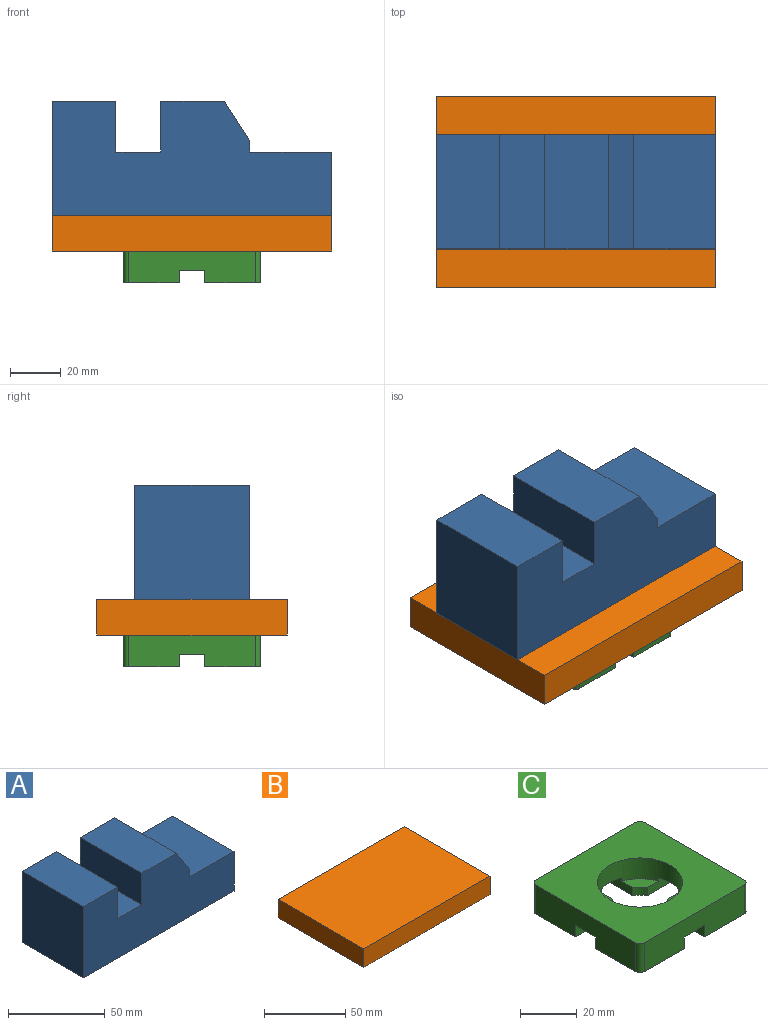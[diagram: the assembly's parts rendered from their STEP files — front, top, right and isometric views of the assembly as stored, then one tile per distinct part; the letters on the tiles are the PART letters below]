
ASSEMBLY  parts=3 mates=2
PART A: 13 faces, bbox 110x45x45 mm
  f0: plane 110x45mm, normal (0,0,-1), area 4950mm2, adj f1,f10,f11,f12
  f1: plane 45x25mm, normal (1,0,0), area 1125mm2, adj f0,f2,f11,f12
  f2: plane 45x32.3mm, normal (0,0,1), area 1453.6mm2, adj f1,f3,f11,f12
  f3: plane 45x4.59mm, normal (1,0,0), area 206.5mm2, adj f2,f4,f11,f12
  f4: plane 45x15.41mm, normal (0.84,0,0.54), area 824.9mm2, adj f3,f5,f11,f12
  f5: plane 45x25.08mm, normal (0,0,1), area 1128.4mm2, adj f4,f6,f11,f12
  f6: plane 45x20mm, normal (-1,0,0), area 900mm2, adj f5,f7,f11,f12
  f7: plane 45x17.7mm, normal (0,0,1), area 796.4mm2, adj f6,f8,f11,f12
  f8: plane 45x20mm, normal (1,0,0), area 900mm2, adj f7,f9,f11,f12
  f9: plane 45x25mm, normal (0,0,1), area 1125mm2, adj f8,f10,f11,f12
  f10: plane 45x45mm, normal (-1,0,0), area 2025mm2, adj f0,f9,f11,f12
  f11: plane 110x45mm, normal (0,-1,0), area 3873.5mm2, adj f0,f1,f2,f3,f4,f5,f6,f7
  f12: plane 110x45mm, normal (0,1,0), area 3873.5mm2, adj f0,f1,f2,f3,f4,f5,f6,f7
PART B: 6 faces, bbox 110x75x14 mm
  f0: plane 75x14mm, normal (-1,0,0), area 1050mm2, adj f1,f3,f4,f5
  f1: plane 110x14mm, normal (0,-1,0), area 1540mm2, adj f0,f2,f4,f5
  f2: plane 75x14mm, normal (1,0,0), area 1050mm2, adj f1,f3,f4,f5
  f3: plane 110x14mm, normal (0,1,0), area 1540mm2, adj f0,f2,f4,f5
  f4: plane 110x75mm, normal (0,0,1), area 8250mm2, adj f0,f1,f2,f3
  f5: plane 110x75mm, normal (0,0,-1), area 8250mm2, adj f0,f1,f2,f3
PART C: 34 faces, bbox 54x54x12.5 mm
  f0: cylinder r=10mm len=3.66mm, axis (0,0,-1), area 18.3mm2, adj f5,f10,f17,f26
  f1: cylinder r=10mm len=3.66mm, axis (0,0,-1), area 18.3mm2, adj f4,f15,f16,f27
  f2: cylinder r=10mm len=3.66mm, axis (0,0,-1), area 18.3mm2, adj f6,f9,f18,f28
  f3: cylinder r=10mm len=3.66mm, axis (0,0,-1), area 18.3mm2, adj f7,f8,f11,f29
  f4: plane 22x22mm, normal (0,0,-1), area 475.3mm2, adj f1,f15,f16,f20,f22,f33
  f5: plane 22x22mm, normal (0,0,-1), area 475.3mm2, adj f0,f10,f17,f21,f22,f32
  f6: plane 22x22mm, normal (0,0,-1), area 475.3mm2, adj f2,f9,f18,f19,f20,f30
  f7: plane 22x22mm, normal (0,0,-1), area 475.3mm2, adj f3,f8,f11,f19,f21,f31
  f8: plane 18.34x5mm, normal (-1,0,0), area 83.5mm2, adj f3,f7,f12,f19,f25,f29
  f9: plane 18.34x5mm, normal (1,0,0), area 83.5mm2, adj f2,f6,f12,f19,f25,f28
  f10: plane 18.34x5mm, normal (0,-1,0), area 83.5mm2, adj f0,f5,f13,f21,f25,f26
  f11: plane 18.34x5mm, normal (0,1,0), area 83.5mm2, adj f3,f7,f13,f21,f25,f29
  f12: plane 12.86x10mm, normal (0,0,-1), area 122.8mm2, adj f8,f9,f19,f25
  f13: plane 12.86x10mm, normal (0,0,-1), area 122.8mm2, adj f10,f11,f21,f25
  f14: plane 12.86x10mm, normal (0,0,-1), area 122.8mm2, adj f16,f17,f22,f25
  f15: plane 18.34x5mm, normal (0,-1,0), area 83.5mm2, adj f1,f4,f20,f24,f25,f27
  f16: plane 18.34x5mm, normal (1,0,0), area 83.5mm2, adj f1,f4,f14,f22,f25,f27
  f17: plane 18.34x5mm, normal (-1,0,0), area 83.5mm2, adj f0,f5,f14,f22,f25,f26
  f18: plane 18.34x5mm, normal (0,1,0), area 83.5mm2, adj f2,f6,f20,f24,f25,f28
  f19: plane 50x12.5mm, normal (0,-1,0), area 575mm2, adj f6,f7,f8,f9,f12,f23,f30,f31
  f20: plane 50x12.5mm, normal (-1,0,0), area 575mm2, adj f4,f6,f15,f18,f23,f24,f30,f33
  f21: plane 50x12.5mm, normal (1,0,0), area 575mm2, adj f5,f7,f10,f11,f13,f23,f31,f32
  f22: plane 50x12.5mm, normal (0,1,0), area 575mm2, adj f4,f5,f14,f16,f17,f23,f32,f33
  f23: plane 54x54mm, normal (0,0,1), area 2205.7mm2, adj f19,f20,f21,f22,f25,f30,f31,f32
  f24: plane 12.86x10mm, normal (0,0,-1), area 122.8mm2, adj f15,f18,f20,f25
  f25: cylinder r=15mm len=30mm, axis (0,0,1), area 787.1mm2, adj f8,f9,f10,f11,f12,f13,f14,f15
  f26: plane 9.14x9.14mm, normal (0,0,1), area 46.7mm2, adj f0,f10,f17,f25
  f27: plane 9.14x9.14mm, normal (0,0,1), area 46.7mm2, adj f1,f15,f16,f25
  f28: plane 9.14x9.14mm, normal (0,0,1), area 46.7mm2, adj f2,f9,f18,f25
  f29: plane 9.14x9.14mm, normal (0,0,1), area 46.7mm2, adj f3,f8,f11,f25
  f30: cylinder r=2mm len=12.5mm, axis (0,0,1), area 39.3mm2, adj f6,f19,f20,f23
  f31: cylinder r=2mm len=12.5mm, axis (0,0,-1), area 39.3mm2, adj f7,f19,f21,f23
  f32: cylinder r=2mm len=12.5mm, axis (0,0,1), area 39.3mm2, adj f5,f21,f22,f23
  f33: cylinder r=2mm len=12.5mm, axis (0,0,-1), area 39.3mm2, adj f4,f20,f22,f23
PLACE A t=(0,0,26.5)mm
PLACE B t=(0,0,12.5)mm
PLACE C at identity fixed
MATE fastened B.f5 <-> C.f0  axis (0,0,-1) through (0,0,12.5)mm
MATE fastened A.f0 <-> B.f4  axis (0,0,-1) through (0,0,26.5)mm
